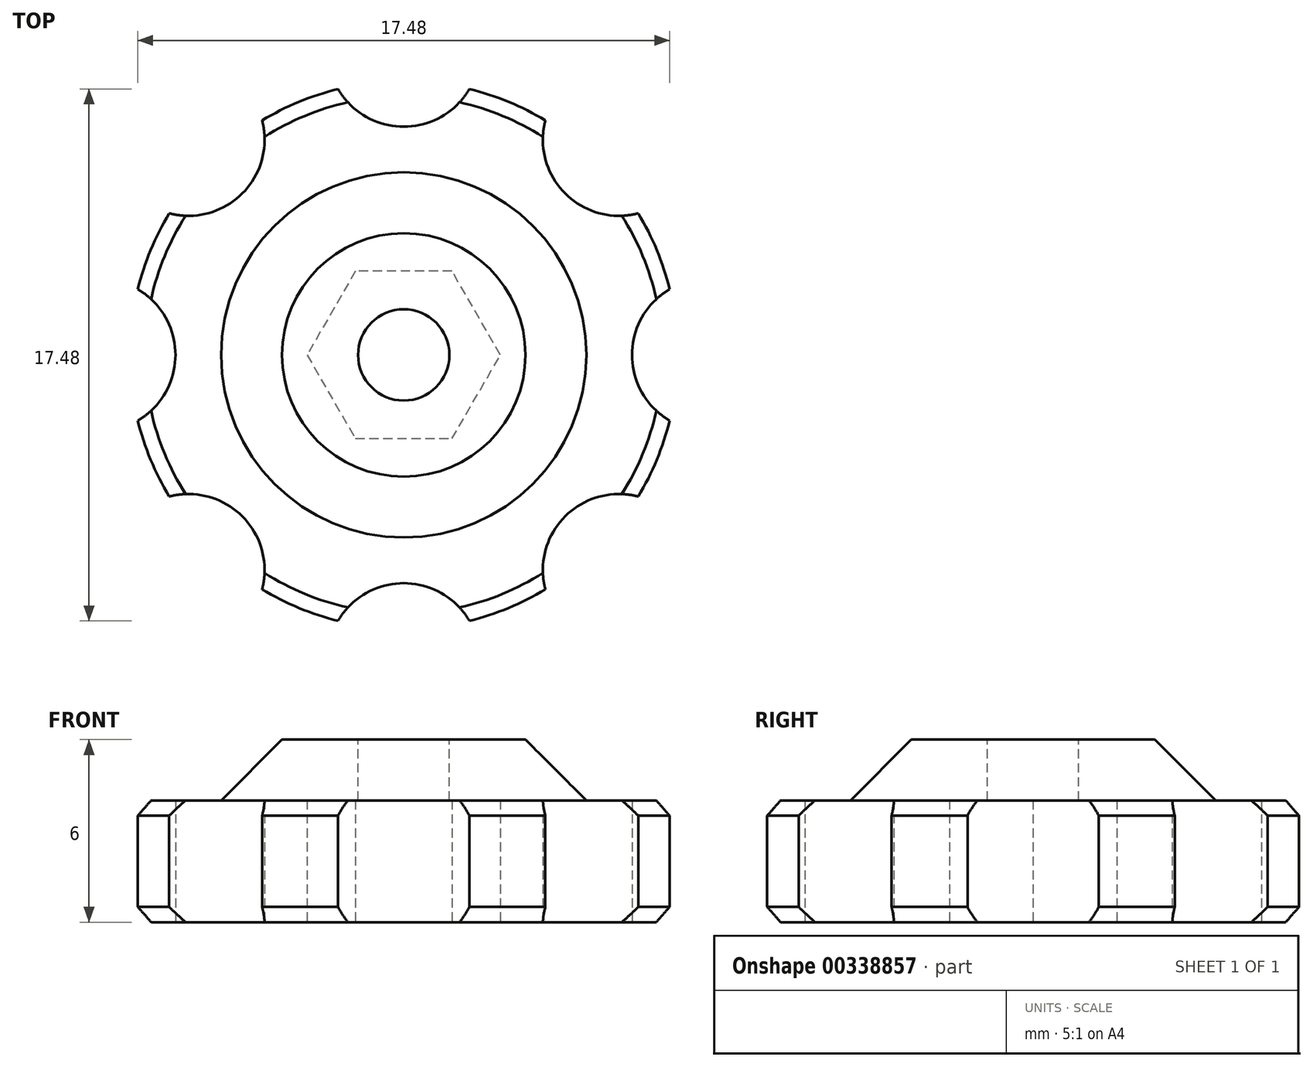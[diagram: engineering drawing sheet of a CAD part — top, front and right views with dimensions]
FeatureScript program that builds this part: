
annotation { "Feature Type Name" : "Feature", "Feature Type Description" : "" }
export const myFeature = defineFeature(function(context is Context, id is Id, definition is map)
    precondition{}
    {
        {
            var Q0;
            Q0=qCreatedBy(makeId("Front.planeOp"),FACE);
            var sketch = newSketch(context, id + "F0", { "sketchPlane" : qUnion([Q0])});
            skLineSegment(sketch, "E0", {"start": v(1.5, 0) * mm, "end": v(1.5, 6) * mm});
            skLineSegment(sketch, "E1", {"start": v(1.5, 6) * mm, "end": v(4, 6) * mm});
            skLineSegment(sketch, "E2", {"start": v(4, 6) * mm, "end": v(6, 4) * mm});
            skLineSegment(sketch, "E3", {"start": v(6, 4) * mm, "end": v(9, 4) * mm});
            skLineSegment(sketch, "E4", {"start": v(9, 4) * mm, "end": v(9, 0) * mm});
            skLineSegment(sketch, "E5", {"start": v(9, 0) * mm, "end": v(1.5, 0) * mm});
            skLineSegment(sketch, "E6", {"start": v(0, 7.74) * mm, "end": v(0, 0) * mm, "construction": true});
            skSolve(sketch);
        }
        {
            var Q0;
            Q0=makeQuery(id+"F0.imprint","IMPRINT",FACE,{"disambiguationData":[TD([[makeQuery(id+"F0.imprint","IMPRINT",EDGE,{"derivedFrom":sQuery(id+"F0.wireOp",EDGE,"E0")}),-1.0]])]});
            var Q1;
            Q1=sQuery(id+"F0.wireOp",EDGE,"E6");
            revolve(context, id + "F1", {"entities" : qUnion([Q0]), "axis" : qUnion([Q1]), "revolveType" : RevolveType.FULL});
        }
        {
            var Q0;
            Q0=qCreatedBy(makeId("Top.planeOp"),FACE);
            var sketch = newSketch(context, id + "F2", { "sketchPlane" : qUnion([Q0])});
            skCircle(sketch, "E7", {"center": v(0, 10) * mm, "radius": 2.5 * mm});
            skSolve(sketch);
        }
        {
            var Q0;
            Q0=makeQuery(id+"F1.opRevolve","SWEPT_EDGE",EDGE,{"disambiguationData":[OSD([sQuery(id+"F0.wireOp",EDGE,"E3"),sQuery(id+"F0.wireOp",EDGE,"E4")])]});
            var Q1;
            Q1=makeQuery(id+"F1.opRevolve","SWEPT_EDGE",EDGE,{"disambiguationData":[OSD([sQuery(id+"F0.wireOp",EDGE,"E4"),sQuery(id+"F0.wireOp",EDGE,"E5")])]});
            chamfer(context, id + "F3", {"entities" : qUnion([Q0, Q1]), "width" : 0.5 * mm, "tangentPropagation" : true});
        }
        {
            var Q0;
            Q0 = qSketchRegion(id + "F2", true);
            var Q1;
            Q1=makeQuery(id+"F1.opRevolve","SWEPT_FACE",FACE,{"disambiguationData":[OSD([sQuery(id+"F0.wireOp",EDGE,"E1")])]});
            extrude(context, id + "F4", {"entities" : qUnion([Q0]), "endBound" : BoundingType.UP_TO_SURFACE, "endBoundEntityFace" : qUnion([Q1]), "depth" : 25 * mm});
        }
        {
            var Q0;
            Q0=makeQuery(id+"F4.opExtrude","SWEPT_BODY",BODY,{"disambiguationData":[OSD([sQuery(id+"F2.wireOp",EDGE,"E7")])]});
            var Q1;
            Q1=makeQuery(id+"F1.opRevolve","SWEPT_FACE",FACE,{"disambiguationData":[OSD([sQuery(id+"F0.wireOp",EDGE,"E0")])]});
            circularPattern(context, id + "F5", {"entities" : qUnion([Q0]), "axis" : qUnion([Q1]), "angle" : 360 * degree, "instanceCount" : 8, "equalSpace" : true});
        }
        {
            var Q0;
            Q0=makeQuery(id+"F4.opExtrude","SWEPT_BODY",BODY,{"disambiguationData":[OSD([sQuery(id+"F2.wireOp",EDGE,"E7")])]});
            var Q1;
            Q1=makeQuery(id+"F5.opPattern","COPY",BODY,{"derivedFrom":makeQuery(id+"F4.opExtrude","SWEPT_BODY",BODY,{"disambiguationData":[OSD([sQuery(id+"F2.wireOp",EDGE,"E7")])]}),"instanceName":"1"});
            var Q2;
            Q2=makeQuery(id+"F5.opPattern","COPY",BODY,{"derivedFrom":makeQuery(id+"F4.opExtrude","SWEPT_BODY",BODY,{"disambiguationData":[OSD([sQuery(id+"F2.wireOp",EDGE,"E7")])]}),"instanceName":"2"});
            var Q3;
            Q3=makeQuery(id+"F5.opPattern","COPY",BODY,{"derivedFrom":makeQuery(id+"F4.opExtrude","SWEPT_BODY",BODY,{"disambiguationData":[OSD([sQuery(id+"F2.wireOp",EDGE,"E7")])]}),"instanceName":"3"});
            var Q4;
            Q4=makeQuery(id+"F5.opPattern","COPY",BODY,{"derivedFrom":makeQuery(id+"F4.opExtrude","SWEPT_BODY",BODY,{"disambiguationData":[OSD([sQuery(id+"F2.wireOp",EDGE,"E7")])]}),"instanceName":"4"});
            var Q5;
            Q5=makeQuery(id+"F5.opPattern","COPY",BODY,{"derivedFrom":makeQuery(id+"F4.opExtrude","SWEPT_BODY",BODY,{"disambiguationData":[OSD([sQuery(id+"F2.wireOp",EDGE,"E7")])]}),"instanceName":"5"});
            var Q6;
            Q6=makeQuery(id+"F5.opPattern","COPY",BODY,{"derivedFrom":makeQuery(id+"F4.opExtrude","SWEPT_BODY",BODY,{"disambiguationData":[OSD([sQuery(id+"F2.wireOp",EDGE,"E7")])]}),"instanceName":"6"});
            var Q7;
            Q7=makeQuery(id+"F5.opPattern","COPY",BODY,{"derivedFrom":makeQuery(id+"F4.opExtrude","SWEPT_BODY",BODY,{"disambiguationData":[OSD([sQuery(id+"F2.wireOp",EDGE,"E7")])]}),"instanceName":"7"});
            var Q8;
            Q8=makeQuery(id+"F1.opRevolve","SWEPT_BODY",BODY,{"disambiguationData":[OSD([sQuery(id+"F0.wireOp",EDGE,"E0"),sQuery(id+"F0.wireOp",EDGE,"E1"),sQuery(id+"F0.wireOp",EDGE,"E2"),sQuery(id+"F0.wireOp",EDGE,"E3"),sQuery(id+"F0.wireOp",EDGE,"E4"),sQuery(id+"F0.wireOp",EDGE,"E5")])]});
            booleanBodies(context, id + "F6", {"operationType" : BooleanOperationType.SUBTRACTION, "tools" : qUnion([Q0, Q1, Q2, Q3, Q4, Q5, Q6, Q7]), "targets" : qUnion([Q8])});
        }
        {
            var Q0;
            Q0=makeQuery(id+"F1.opRevolve","SWEPT_FACE",FACE,{"disambiguationData":[OSD([sQuery(id+"F0.wireOp",EDGE,"E5")])]});
            var sketch = newSketch(context, id + "F7", { "sketchPlane" : qUnion([Q0])});
            skCircle(sketch, "E8.cCircle", {"center": v(0, 0) * mm, "radius": 3.18 * mm, "construction": true});
            skLineSegment(sketch, "E8.0", {"start": v(-3.18, 0) * mm, "end": v(-1.59, 2.75) * mm});
            skLineSegment(sketch, "E8.1", {"start": v(-1.59, 2.75) * mm, "end": v(1.59, 2.75) * mm});
            skLineSegment(sketch, "E8.2", {"start": v(1.59, 2.75) * mm, "end": v(3.18, 0) * mm});
            skLineSegment(sketch, "E8.3", {"start": v(3.18, 0) * mm, "end": v(1.59, -2.75) * mm});
            skLineSegment(sketch, "E8.4", {"start": v(1.59, -2.75) * mm, "end": v(-1.59, -2.75) * mm});
            skLineSegment(sketch, "E8.5", {"start": v(-1.59, -2.75) * mm, "end": v(-3.18, 0) * mm});
            skSolve(sketch);
        }
        {
            var Q0;
            Q0 = qSketchRegion(id + "F7", true);
            extrude(context, id + "F8", {"entities" : qUnion([Q0]), "operationType" : NewBodyOperationType.REMOVE, "oppositeDirection" : true, "depth" : 4 * mm});
        }
    });
